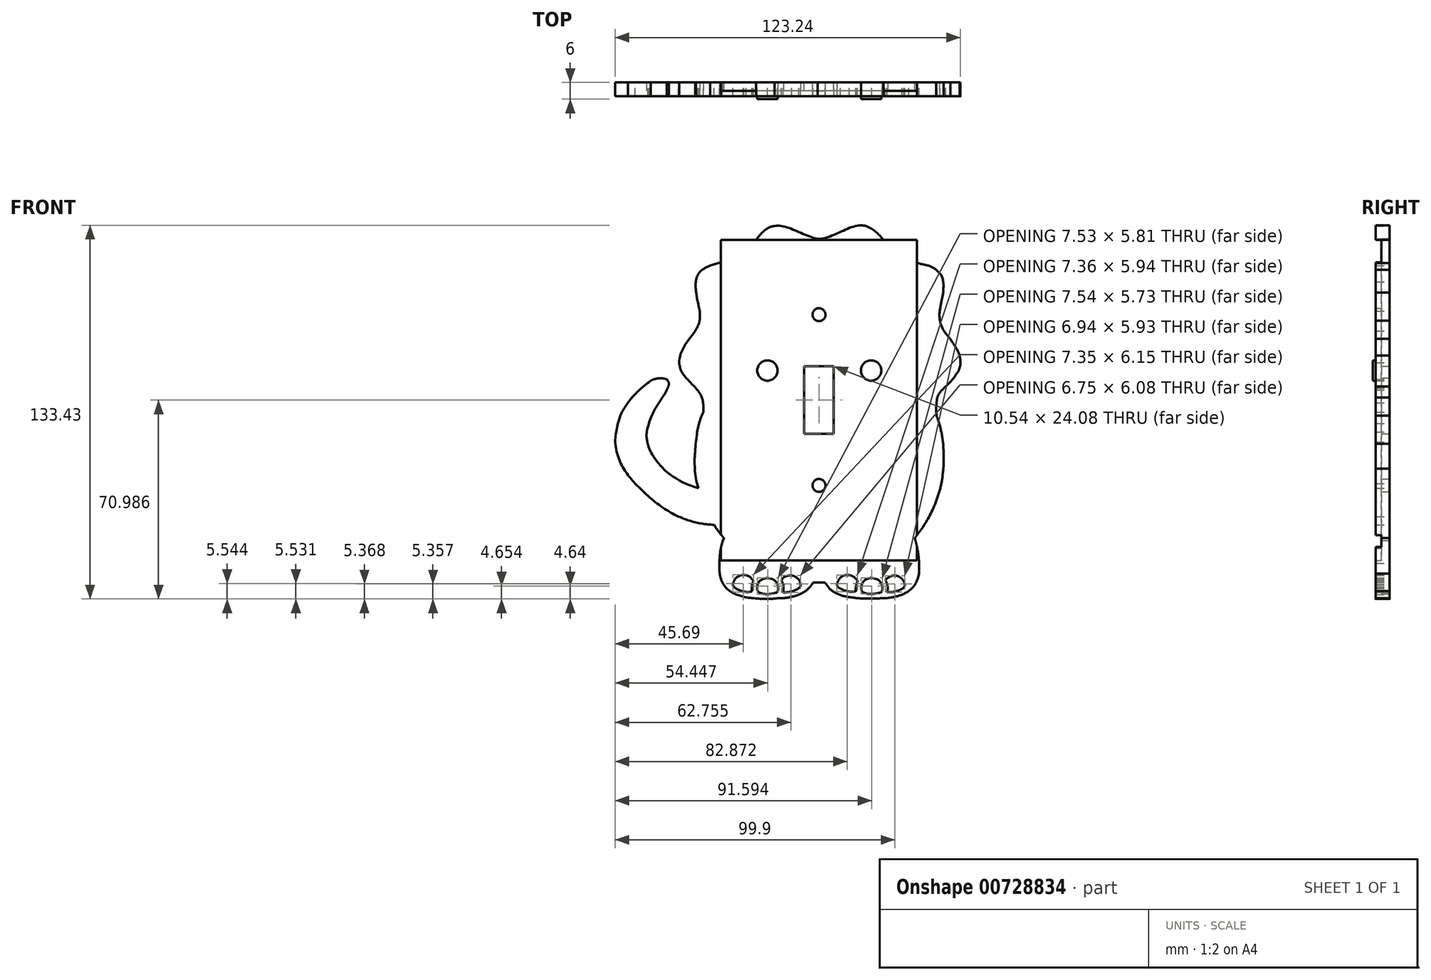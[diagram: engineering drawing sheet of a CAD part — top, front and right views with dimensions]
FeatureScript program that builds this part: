
annotation { "Feature Type Name" : "Feature", "Feature Type Description" : "" }
export const myFeature = defineFeature(function(context is Context, id is Id, definition is map)
    precondition{}
    {
        {
            var Q0;
            Q0=qCreatedBy(makeId("Front.planeOp"),FACE);
            var sketch = newSketch(context, id + "F0", { "sketchPlane" : qUnion([Q0])});
            skPoint(sketch, "E0.1.internal.snap0", {"position": v(2.99, 59.78) * mm});
            skFitSpline(sketch, "E0", {"points": [v(-7.47, 49.47) * mm, v(2.99, 58.9) * mm], "startDerivative": vector(10.46, 9.43) * mm, "endDerivative": vector(13.1, 0.69) * mm});
            skFitSpline(sketch, "E1", {"points": [v(2.99, 58.9) * mm, v(18.4, 54.3) * mm], "startDerivative": vector(13.1, 2.67) * mm, "endDerivative": vector(14.14, -2.41) * mm});
            skFitSpline(sketch, "E2", {"points": [v(18.4, 54.3) * mm, v(33.86, 59.2) * mm], "startDerivative": vector(12.35, -1.3) * mm, "endDerivative": vector(15.18, 0.82) * mm});
            skFitSpline(sketch, "E3", {"points": [v(33.86, 59.2) * mm, v(46.37, 48.8) * mm], "startDerivative": vector(18.66, -1.85) * mm, "endDerivative": vector(12.51, -10.4) * mm});
            skFitSpline(sketch, "E4", {"points": [v(46.37, 48.8) * mm, v(60.6, 43.21) * mm], "startDerivative": vector(10.09, -10.4) * mm, "endDerivative": vector(4.92, -7.38) * mm});
            skFitSpline(sketch, "E5", {"points": [v(60.6, 43.21) * mm, v(63.13, 35.15) * mm], "startDerivative": vector(4.1, -3.7) * mm, "endDerivative": vector(-1.85, -18.66) * mm});
            skFitSpline(sketch, "E6", {"points": [v(63.13, 35.15) * mm, v(62.04, 25.1) * mm], "startDerivative": vector(-2.67, -16) * mm, "endDerivative": vector(1.85, -9.02) * mm});
            skFitSpline(sketch, "E7", {"points": [v(62.04, 25.1) * mm, v(65.68, 18.57) * mm], "startDerivative": vector(0.44, -6.78) * mm, "endDerivative": vector(4.27, -4.63) * mm});
            skFitSpline(sketch, "E8", {"points": [v(65.68, 18.57) * mm, v(69.01, 12.62) * mm], "startDerivative": vector(3.45, -5.92) * mm, "endDerivative": vector(1.74, -6.36) * mm});
            skFitSpline(sketch, "E9", {"points": [v(69.01, 12.62) * mm, v(68.2, 6.5) * mm], "startDerivative": vector(1.74, -7.59) * mm, "endDerivative": vector(-3.49, -5.43) * mm});
            skFitSpline(sketch, "E10", {"points": [v(68.2, 6.5) * mm, v(64.02, 1.58) * mm], "startDerivative": vector(-3.8, -5.95) * mm, "endDerivative": vector(-4.82, -4.3) * mm});
            skFitSpline(sketch, "E11", {"points": [v(64.02, 1.58) * mm, v(61.05, -2.36) * mm], "startDerivative": vector(-3.18, -3.08) * mm, "endDerivative": vector(-2.05, -5.74) * mm});
            skFitSpline(sketch, "E12", {"points": [v(61.05, -2.36) * mm, v(60.74, -8.85) * mm], "startDerivative": vector(-1.44, -7.28) * mm, "endDerivative": vector(0.1, -6.15) * mm});
            skFitSpline(sketch, "E13", {"points": [v(60.74, -8.85) * mm, v(63.17, -18.86) * mm], "startDerivative": vector(4.2, -9.95) * mm, "endDerivative": vector(1.44, -10.87) * mm});
            skFitSpline(sketch, "E14", {"points": [v(63.17, -18.86) * mm, v(63.17, -27.79) * mm], "startDerivative": vector(0.41, -10.15) * mm, "endDerivative": vector(-1.13, -8.61) * mm});
            skFitSpline(sketch, "E15", {"points": [v(63.17, -27.79) * mm, v(61.32, -37.36) * mm], "startDerivative": vector(-0.92, -12.61) * mm, "endDerivative": vector(-2.97, -9.13) * mm});
            skFitSpline(sketch, "E16", {"points": [v(61.32, -37.36) * mm, v(53.02, -52.53) * mm], "startDerivative": vector(-6.56, -20.4) * mm, "endDerivative": vector(-9.74, -12.82) * mm});
            skFitSpline(sketch, "E17", {"points": [v(53.02, -52.53) * mm, v(54.52, -65.21) * mm], "startDerivative": vector(3.9, -13.33) * mm, "endDerivative": vector(-0.62, -12.82) * mm});
            skFitSpline(sketch, "E18", {"points": [v(54.52, -65.21) * mm, v(50.86, -71.38) * mm], "startDerivative": vector(-1.7, -7.76) * mm, "endDerivative": vector(-7.07, -5.24) * mm});
            skFitSpline(sketch, "E19", {"points": [v(50.86, -71.38) * mm, v(43.17, -73.94) * mm], "startDerivative": vector(-6.4, -4.5) * mm, "endDerivative": vector(-10.3, -1.38) * mm});
            skFitSpline(sketch, "E20", {"points": [v(43.17, -73.94) * mm, v(32.13, -73.94) * mm], "startDerivative": vector(-10.66, -0.22) * mm, "endDerivative": vector(-10.66, 1.1) * mm});
            skFitSpline(sketch, "E21", {"points": [v(32.13, -73.94) * mm, v(24.22, -71.74) * mm], "startDerivative": vector(-9.5, 1.45) * mm, "endDerivative": vector(-7.18, 4.79) * mm});
            skFitSpline(sketch, "E22", {"points": [v(24.22, -71.74) * mm, v(21.06, -68.38) * mm], "startDerivative": vector(-4.86, 2.54) * mm, "endDerivative": vector(-2.97, 4.57) * mm});
            skLineSegment(sketch, "E23", {"start": v(21.06, -68.38) * mm, "end": v(16.68, -68.38) * mm});
            skFitSpline(sketch, "E24", {"points": [v(16.68, -68.38) * mm, v(11.67, -72.71) * mm], "startDerivative": vector(-3.8, -7.05) * mm, "endDerivative": vector(-6.24, -2.76) * mm});
            skFitSpline(sketch, "E25", {"points": [v(11.67, -72.71) * mm, v(3.96, -73.97) * mm], "startDerivative": vector(-7.1, -2.4) * mm, "endDerivative": vector(-11.17, 0.22) * mm});
            skFitSpline(sketch, "E26", {"points": [v(3.96, -73.97) * mm, v(-7.2, -73.69) * mm], "startDerivative": vector(-11.87, -1.84) * mm, "endDerivative": vector(-8.77, 0.94) * mm});
            skFitSpline(sketch, "E27", {"points": [v(-7.2, -73.69) * mm, v(-15.71, -68.27) * mm], "startDerivative": vector(-9.72, 2.25) * mm, "endDerivative": vector(-5.3, 10.8) * mm});
            skFitSpline(sketch, "E28", {"points": [v(-15.71, -68.27) * mm, v(-16.73, -61.48) * mm], "startDerivative": vector(-2.76, 5.8) * mm, "endDerivative": vector(0.22, 7.03) * mm});
            skFitSpline(sketch, "E29", {"points": [v(-16.73, -61.48) * mm, v(-15.45, -53.36) * mm], "startDerivative": vector(0.5, 8.05) * mm, "endDerivative": vector(3.12, 9.06) * mm});
            skFitSpline(sketch, "E30", {"points": [v(-15.45, -53.36) * mm, v(-15.1, -52.54) * mm], "startDerivative": vector(0.34, 0.82) * mm, "endDerivative": vector(0.34, 0.82) * mm});
            skFitSpline(sketch, "E31", {"points": [v(-15.1, -52.54) * mm, v(-18.6, -47.79) * mm], "startDerivative": vector(-3.38, 4.36) * mm, "endDerivative": vector(-3.08, 5.43) * mm});
            skFitSpline(sketch, "E32", {"points": [v(-18.6, -47.79) * mm, v(-31.3, -44.81) * mm], "startDerivative": vector(-13.02, 0.56) * mm, "endDerivative": vector(-13.07, 5.8) * mm});
            skFitSpline(sketch, "E33", {"points": [v(-31.3, -44.81) * mm, v(-46.76, -33.1) * mm], "startDerivative": vector(-17.4, 8) * mm, "endDerivative": vector(-15.22, 15.29) * mm});
            skFitSpline(sketch, "E34", {"points": [v(-46.76, -33.1) * mm, v(-53.92, -18.17) * mm], "startDerivative": vector(-10.19, 11.75) * mm, "endDerivative": vector(-2.05, 21.53) * mm});
            skFitSpline(sketch, "E35", {"points": [v(-53.92, -18.17) * mm, v(-49.34, -4.22) * mm], "startDerivative": vector(1.03, 16.61) * mm, "endDerivative": vector(8.82, 10.87) * mm});
            skFitSpline(sketch, "E36", {"points": [v(-49.34, -4.22) * mm, v(-41.18, 3.68) * mm], "startDerivative": vector(7.03, 9.69) * mm, "endDerivative": vector(10, 7.44) * mm});
            skFitSpline(sketch, "E37", {"points": [v(-41.18, 3.68) * mm, v(-35.45, 4.13) * mm], "startDerivative": vector(8.3, 3.9) * mm, "endDerivative": vector(4.15, -1.46) * mm});
            skFitSpline(sketch, "E38", {"points": [v(-35.45, 4.13) * mm, v(-35.45, 0.39) * mm], "startDerivative": vector(3.66, -4.27) * mm, "endDerivative": vector(-1.83, -4.15) * mm});
            skFitSpline(sketch, "E39", {"points": [v(-35.45, 0.39) * mm, v(-41.87, -11.64) * mm], "startDerivative": vector(-6.42, -12.03) * mm, "endDerivative": vector(-4.51, -15.6) * mm});
            skFitSpline(sketch, "E40", {"points": [v(-41.87, -11.64) * mm, v(-42.28, -18.96) * mm], "startDerivative": vector(-3.66, -10) * mm, "endDerivative": vector(1.34, -6.59) * mm});
            skFitSpline(sketch, "E41", {"points": [v(-42.28, -18.96) * mm, v(-24.19, -34.7) * mm], "startDerivative": vector(2.68, -11.22) * mm, "endDerivative": vector(36.1, -9.88) * mm});
            skFitSpline(sketch, "E42", {"points": [v(-24.19, -34.7) * mm, v(-24.65, -14.6) * mm], "startDerivative": vector(-6.62, 19.8) * mm, "endDerivative": vector(2.32, 20.45) * mm});
            skFitSpline(sketch, "E43", {"points": [v(-24.65, -14.6) * mm, v(-22.43, -7.5) * mm], "startDerivative": vector(1.45, 7.54) * mm, "endDerivative": vector(3.2, 6.24) * mm});
            skFitSpline(sketch, "E44", {"points": [v(-22.43, -7.5) * mm, v(-25.04, 0.92) * mm], "startDerivative": vector(-0.15, 9.14) * mm, "endDerivative": vector(-8.85, 9.72) * mm});
            skFitSpline(sketch, "E45", {"points": [v(-25.04, 0.92) * mm, v(-31.08, 10.15) * mm], "startDerivative": vector(-17.7, 18.7) * mm, "endDerivative": vector(-2.32, 11.46) * mm});
            skFitSpline(sketch, "E46", {"points": [v(-31.08, 10.15) * mm, v(-25.33, 21.46) * mm], "startDerivative": vector(1.02, 15.52) * mm, "endDerivative": vector(6.24, 9.43) * mm});
            skFitSpline(sketch, "E47", {"points": [v(-25.33, 21.46) * mm, v(-23.69, 28.52) * mm], "startDerivative": vector(2.9, 5.51) * mm, "endDerivative": vector(-0.87, 12.62) * mm});
            skFitSpline(sketch, "E48", {"points": [v(-23.69, 28.52) * mm, v(-25.14, 38.96) * mm], "startDerivative": vector(-2.76, 12.04) * mm, "endDerivative": vector(0.73, 9.72) * mm});
            skFitSpline(sketch, "E49", {"points": [v(-25.14, 38.96) * mm, v(-19.97, 44.76) * mm], "startDerivative": vector(1.89, 12.9) * mm, "endDerivative": vector(6.38, 3.2) * mm});
            skFitSpline(sketch, "E50", {"points": [v(-19.97, 44.76) * mm, v(-9.67, 47.85) * mm], "startDerivative": vector(10.44, 3.77) * mm, "endDerivative": vector(8.7, 3.77) * mm});
            skFitSpline(sketch, "E51", {"points": [v(-9.67, 47.85) * mm, v(-7.47, 49.47) * mm], "startDerivative": vector(2.61, 0.73) * mm, "endDerivative": vector(2.2, 1.61) * mm});
            skFitSpline(sketch, "E52", {"points": [v(-11.9, -69.22) * mm, v(-8.18, -65.64) * mm], "startDerivative": vector(0.92, 4.72) * mm, "endDerivative": vector(8.61, 1.13) * mm});
            skFitSpline(sketch, "E53", {"points": [v(-7.94, -65.64) * mm, v(-4.56, -67.96) * mm], "startDerivative": vector(3.38, -0.41) * mm, "endDerivative": vector(2.77, -5.54) * mm});
            skFitSpline(sketch, "E54", {"points": [v(-4.56, -67.96) * mm, v(-5.03, -71.41) * mm], "startDerivative": vector(-2.46, -4.92) * mm, "endDerivative": vector(0.72, -2.77) * mm});
            skFitSpline(sketch, "E55", {"points": [v(-5.03, -71.41) * mm, v(-11.9, -69.22) * mm], "startDerivative": vector(-5.33, -3.7) * mm, "endDerivative": vector(-0.1, 4.1) * mm});
            skFitSpline(sketch, "E56", {"points": [v(-3.19, -71.14) * mm, v(0.43, -66.7) * mm], "startDerivative": vector(-1.85, 12) * mm, "endDerivative": vector(2.15, 0.62) * mm});
            skFitSpline(sketch, "E57", {"points": [v(0.43, -66.7) * mm, v(4.1, -71.51) * mm], "startDerivative": vector(14.25, -1.85) * mm, "endDerivative": vector(-0.72, -1.03) * mm});
            skFitSpline(sketch, "E58", {"points": [v(-3.19, -71.14) * mm, v(4.1, -71.51) * mm], "startDerivative": vector(3.38, -7.28) * mm, "endDerivative": vector(-0.92, 2.05) * mm});
            skFitSpline(sketch, "E59", {"points": [v(6.07, -71.93) * mm, v(12.2, -69.87) * mm], "startDerivative": vector(7.7, -0.1) * mm, "endDerivative": vector(2.77, 3.49) * mm});
            skFitSpline(sketch, "E60", {"points": [v(12.2, -69.87) * mm, v(9.05, -65.84) * mm], "startDerivative": vector(-0.1, 1.95) * mm, "endDerivative": vector(-11.18, 2.97) * mm});
            skFitSpline(sketch, "E61", {"points": [v(9.05, -65.84) * mm, v(5.46, -67.65) * mm], "startDerivative": vector(-4.3, -0.1) * mm, "endDerivative": vector(-2.56, -5.02) * mm});
            skFitSpline(sketch, "E62", {"points": [v(5.46, -67.65) * mm, v(6.07, -71.93) * mm], "startDerivative": vector(1.74, -3.59) * mm, "endDerivative": vector(-1.13, -7.8) * mm});
            skFitSpline(sketch, "E63", {"points": [v(25.28, -68.99) * mm, v(29.63, -65.74) * mm], "startDerivative": vector(-0.1, 1.64) * mm, "endDerivative": vector(10.25, -1.33) * mm});
            skFitSpline(sketch, "E64", {"points": [v(29.63, -65.74) * mm, v(32.63, -68.03) * mm], "startDerivative": vector(1.74, 0.1) * mm, "endDerivative": vector(2.36, -5.13) * mm});
            skFitSpline(sketch, "E65", {"points": [v(32.63, -68.03) * mm, v(32.12, -71.45) * mm], "startDerivative": vector(-1.23, -1.85) * mm, "endDerivative": vector(1.33, -3.8) * mm});
            skFitSpline(sketch, "E66", {"points": [v(25.28, -68.99) * mm, v(26.43, -70.55) * mm], "startDerivative": vector(-0.47, -2.95) * mm, "endDerivative": vector(1.33, -0.77) * mm});
            skFitSpline(sketch, "E67", {"points": [v(26.43, -70.55) * mm, v(32.12, -71.45) * mm], "startDerivative": vector(6.56, -3.44) * mm, "endDerivative": vector(4.83, 1.36) * mm});
            skFitSpline(sketch, "E68", {"points": [v(33.98, -71.13) * mm, v(37.7, -66.72) * mm], "startDerivative": vector(-0.87, 3.08) * mm, "endDerivative": vector(11.33, 0.77) * mm});
            skFitSpline(sketch, "E69", {"points": [v(37.7, -66.72) * mm, v(41.35, -71.35) * mm], "startDerivative": vector(12.87, -1.54) * mm, "endDerivative": vector(-0.46, -2.2) * mm});
            skFitSpline(sketch, "E70", {"points": [v(33.98, -71.13) * mm, v(41.35, -71.35) * mm], "startDerivative": vector(2.82, -7.13) * mm, "endDerivative": vector(-1.7, 2.36) * mm});
            skFitSpline(sketch, "E71", {"points": [v(42.5, -67.52) * mm, v(48.5, -67.08) * mm], "startDerivative": vector(1.23, 1.18) * mm, "endDerivative": vector(9.59, -8.25) * mm});
            skFitSpline(sketch, "E72", {"points": [v(48.5, -67.08) * mm, v(49.09, -70.2) * mm], "startDerivative": vector(1.9, -2.56) * mm, "endDerivative": vector(-2.61, -3.38) * mm});
            skFitSpline(sketch, "E73", {"points": [v(49.09, -70.2) * mm, v(43.1, -71.81) * mm], "startDerivative": vector(-5.02, -3.49) * mm, "endDerivative": vector(-7.74, 0.46) * mm});
            skFitSpline(sketch, "E74", {"points": [v(42.5, -67.52) * mm, v(43.1, -71.81) * mm], "startDerivative": vector(1.54, -2.56) * mm, "endDerivative": vector(-1.9, -4.77) * mm});
            skEllipse(sketch, "E75", {"center": v(14.47, -19.48) * mm, "majorRadius": 3.3 * mm, "minorRadius": 2.54 * mm, "majorAxis": v(-0.41, 0.91)});
            skEllipse(sketch, "E76", {"center": v(23.22, -19.68) * mm, "majorRadius": 3.36 * mm, "minorRadius": 2.42 * mm, "majorAxis": v(0.55, 0.84)});
            skFitSpline(sketch, "E77", {"points": [v(18.8, -2.75) * mm, v(15.96, -12.8) * mm], "startDerivative": vector(-5.6, -9.76) * mm, "endDerivative": vector(1.95, -11.34) * mm});
            skFitSpline(sketch, "E78", {"points": [v(18.8, -2.75) * mm, v(21.85, -12.67) * mm], "startDerivative": vector(5.6, -8.54) * mm, "endDerivative": vector(-1.1, -12.68) * mm});
            skFitSpline(sketch, "E79", {"points": [v(15.96, -12.8) * mm, v(21.85, -12.67) * mm], "startDerivative": vector(9.63, -9.88) * mm, "endDerivative": vector(2.32, 2.68) * mm});
            skCircle(sketch, "E80", {"center": v(37.44, 7.3) * mm, "radius": 8.13 * mm});
            skPoint(sketch, "E80.first.point", {"position": v(35.22, 15.12) * mm});
            skPoint(sketch, "E80.second.point", {"position": v(39.45, -0.57) * mm});
            skPoint(sketch, "E80.third.point", {"position": v(31.4, 1.86) * mm});
            skCircle(sketch, "E81", {"center": v(0.43, 7.3) * mm, "radius": 8.13 * mm});
            skFitSpline(sketch, "E82", {"points": [v(-0.95, 42.83) * mm, v(9.53, 27.7) * mm], "startDerivative": vector(11.46, -7.32) * mm, "endDerivative": vector(3.41, -21.46) * mm});
            skFitSpline(sketch, "E83", {"points": [v(-0.95, 42.83) * mm, v(-0.95, 25.1) * mm], "startDerivative": vector(-9.02, -23.41) * mm, "endDerivative": vector(2.68, -10.73) * mm});
            skFitSpline(sketch, "E84", {"points": [v(-0.95, 25.1) * mm, v(9.53, 27.7) * mm], "startDerivative": vector(8.54, -7.56) * mm, "endDerivative": vector(7.07, 18.3) * mm});
            skFitSpline(sketch, "E85", {"points": [v(39.04, 42.83) * mm, v(37.99, 24.38) * mm], "startDerivative": vector(7.56, -22.44) * mm, "endDerivative": vector(-4.88, -4.63) * mm});
            skFitSpline(sketch, "E86", {"points": [v(39.04, 42.83) * mm, v(28.31, 28.2) * mm], "startDerivative": vector(-5.6, 0.24) * mm, "endDerivative": vector(-4.15, -21.95) * mm});
            skFitSpline(sketch, "E87", {"points": [v(28.31, 28.2) * mm, v(37.99, 24.38) * mm], "startDerivative": vector(6.59, -21.22) * mm, "endDerivative": vector(4.88, 3.66) * mm});
            skFitSpline(sketch, "E88", {"points": [v(-8.18, -65.64) * mm, v(-7.94, -65.64) * mm], "startDerivative": vector(0.24, 0) * mm, "endDerivative": vector(0.24, 0) * mm});
            skSolve(sketch);
        }
        {
            var Q0;
            Q0 = qSketchRegion(id + "F0", true);
            extrude(context, id + "F1", {"entities" : qUnion([Q0]), "depth" : 5 * mm, "offsetDistance" : 25 * mm});
        }
        {
            var Q0;
            Q0=makeQuery(id+"F1.opExtrude","CAP_FACE",FACE,{"disambiguationData":[OSD([sQuery(id+"F0.wireOp",EDGE,"E0"),sQuery(id+"F0.wireOp",EDGE,"E1"),sQuery(id+"F0.wireOp",EDGE,"E2"),sQuery(id+"F0.wireOp",EDGE,"E3"),sQuery(id+"F0.wireOp",EDGE,"E4"),sQuery(id+"F0.wireOp",EDGE,"E5"),sQuery(id+"F0.wireOp",EDGE,"E6"),sQuery(id+"F0.wireOp",EDGE,"E7"),sQuery(id+"F0.wireOp",EDGE,"E8"),sQuery(id+"F0.wireOp",EDGE,"E9"),sQuery(id+"F0.wireOp",EDGE,"E10"),sQuery(id+"F0.wireOp",EDGE,"E11"),sQuery(id+"F0.wireOp",EDGE,"E12"),sQuery(id+"F0.wireOp",EDGE,"E13"),sQuery(id+"F0.wireOp",EDGE,"E14"),sQuery(id+"F0.wireOp",EDGE,"E15"),sQuery(id+"F0.wireOp",EDGE,"E16"),sQuery(id+"F0.wireOp",EDGE,"E17"),sQuery(id+"F0.wireOp",EDGE,"E18"),sQuery(id+"F0.wireOp",EDGE,"E19"),sQuery(id+"F0.wireOp",EDGE,"E20"),sQuery(id+"F0.wireOp",EDGE,"E21"),sQuery(id+"F0.wireOp",EDGE,"E22"),sQuery(id+"F0.wireOp",EDGE,"E23"),sQuery(id+"F0.wireOp",EDGE,"E24"),sQuery(id+"F0.wireOp",EDGE,"E25"),sQuery(id+"F0.wireOp",EDGE,"E26"),sQuery(id+"F0.wireOp",EDGE,"E27"),sQuery(id+"F0.wireOp",EDGE,"E28"),sQuery(id+"F0.wireOp",EDGE,"E29"),sQuery(id+"F0.wireOp",EDGE,"E30"),sQuery(id+"F0.wireOp",EDGE,"E31"),sQuery(id+"F0.wireOp",EDGE,"E32"),sQuery(id+"F0.wireOp",EDGE,"E33"),sQuery(id+"F0.wireOp",EDGE,"E34"),sQuery(id+"F0.wireOp",EDGE,"E35"),sQuery(id+"F0.wireOp",EDGE,"E36"),sQuery(id+"F0.wireOp",EDGE,"E37"),sQuery(id+"F0.wireOp",EDGE,"E38"),sQuery(id+"F0.wireOp",EDGE,"E39"),sQuery(id+"F0.wireOp",EDGE,"E40"),sQuery(id+"F0.wireOp",EDGE,"E41"),sQuery(id+"F0.wireOp",EDGE,"E42"),sQuery(id+"F0.wireOp",EDGE,"E43"),sQuery(id+"F0.wireOp",EDGE,"E44"),sQuery(id+"F0.wireOp",EDGE,"E45"),sQuery(id+"F0.wireOp",EDGE,"E46"),sQuery(id+"F0.wireOp",EDGE,"E47"),sQuery(id+"F0.wireOp",EDGE,"E48"),sQuery(id+"F0.wireOp",EDGE,"E49"),sQuery(id+"F0.wireOp",EDGE,"E50"),sQuery(id+"F0.wireOp",EDGE,"E51"),sQuery(id+"F0.wireOp",EDGE,"E52"),sQuery(id+"F0.wireOp",EDGE,"E53"),sQuery(id+"F0.wireOp",EDGE,"E54"),sQuery(id+"F0.wireOp",EDGE,"E55"),sQuery(id+"F0.wireOp",EDGE,"E56"),sQuery(id+"F0.wireOp",EDGE,"E57"),sQuery(id+"F0.wireOp",EDGE,"E58"),sQuery(id+"F0.wireOp",EDGE,"E59"),sQuery(id+"F0.wireOp",EDGE,"E60"),sQuery(id+"F0.wireOp",EDGE,"E61"),sQuery(id+"F0.wireOp",EDGE,"E62"),sQuery(id+"F0.wireOp",EDGE,"E63"),sQuery(id+"F0.wireOp",EDGE,"E64"),sQuery(id+"F0.wireOp",EDGE,"E65"),sQuery(id+"F0.wireOp",EDGE,"E66"),sQuery(id+"F0.wireOp",EDGE,"E67"),sQuery(id+"F0.wireOp",EDGE,"E68"),sQuery(id+"F0.wireOp",EDGE,"E69"),sQuery(id+"F0.wireOp",EDGE,"E70"),sQuery(id+"F0.wireOp",EDGE,"E71"),sQuery(id+"F0.wireOp",EDGE,"E72"),sQuery(id+"F0.wireOp",EDGE,"E73"),sQuery(id+"F0.wireOp",EDGE,"E74"),sQuery(id+"F0.wireOp",EDGE,"E75"),sQuery(id+"F0.wireOp",EDGE,"E76"),sQuery(id+"F0.wireOp",EDGE,"E77"),sQuery(id+"F0.wireOp",EDGE,"E78"),sQuery(id+"F0.wireOp",EDGE,"E79"),sQuery(id+"F0.wireOp",EDGE,"E80"),sQuery(id+"F0.wireOp",EDGE,"E81"),sQuery(id+"F0.wireOp",EDGE,"E82"),sQuery(id+"F0.wireOp",EDGE,"E83"),sQuery(id+"F0.wireOp",EDGE,"E84"),sQuery(id+"F0.wireOp",EDGE,"E85"),sQuery(id+"F0.wireOp",EDGE,"E86"),sQuery(id+"F0.wireOp",EDGE,"E87"),sQuery(id+"F0.wireOp",EDGE,"E88")])],"isStart":true});
            var sketch = newSketch(context, id + "F2", { "sketchPlane" : qUnion([Q0])});
            skLineSegment(sketch, "E89.bottom", {"start": v(-24.1, 8.79) * mm, "end": v(-24.1, -15.3) * mm});
            skLineSegment(sketch, "E89.top", {"start": v(-13.57, 8.79) * mm, "end": v(-13.57, -15.3) * mm});
            skLineSegment(sketch, "E89.left", {"start": v(-24.1, 8.79) * mm, "end": v(-13.57, 8.79) * mm});
            skLineSegment(sketch, "E89.right", {"start": v(-24.1, -15.3) * mm, "end": v(-13.57, -15.3) * mm});
            skCircle(sketch, "E90", {"center": v(-18.84, -33.73) * mm, "radius": 2.31 * mm});
            skLineSegment(sketch, "E91", {"start": v(-55.14, -3.25) * mm, "end": v(34, -3.25) * mm, "construction": true});
            skLineSegment(sketch, "E92", {"start": v(-53.8, -3.25) * mm, "end": v(-53.8, -60.49) * mm});
            skLineSegment(sketch, "E93", {"start": v(-53.8, -60.49) * mm, "end": v(16.19, -60.49) * mm});
            skLineSegment(sketch, "E94", {"start": v(16.19, -60.49) * mm, "end": v(16.19, -3.25) * mm});
            skLineSegment(sketch, "E95.MirrorCS", {"start": v(-53.8, -3.25) * mm, "end": v(-53.8, 53.98) * mm});
            skLineSegment(sketch, "E96.MirrorCS", {"start": v(-53.8, 53.98) * mm, "end": v(16.19, 53.98) * mm});
            skLineSegment(sketch, "E97.MirrorCS", {"start": v(16.19, 53.98) * mm, "end": v(16.19, -3.25) * mm});
            skCircle(sketch, "E98.MirrorC", {"center": v(-18.84, 27.23) * mm, "radius": 2.31 * mm});
            skSolve(sketch);
        }
        {
            var Q0;
            Q0=makeQuery(id+"F2.imprint","IMPRINT",FACE,{"disambiguationData":[TD([[makeQuery(id+"F2.imprint","IMPRINT",EDGE,{"derivedFrom":sQuery(id+"F2.wireOp",EDGE,"E89.bottom")}),1.0]])]});
            var Q1;
            Q1=makeQuery(id+"F2.imprint","IMPRINT",FACE,{"disambiguationData":[TD([[makeQuery(id+"F2.imprint","IMPRINT",EDGE,{"derivedFrom":sQuery(id+"F2.wireOp",EDGE,"E98.MirrorC")}),-1.0]])]});
            var Q2;
            Q2=makeQuery(id+"F2.imprint","IMPRINT",FACE,{"disambiguationData":[TD([[makeQuery(id+"F2.imprint","IMPRINT",EDGE,{"derivedFrom":sQuery(id+"F2.wireOp",EDGE,"E90")}),1.0]])]});
            extrude(context, id + "F3", {"entities" : qUnion([Q0, Q1, Q2]), "operationType" : NewBodyOperationType.REMOVE, "oppositeDirection" : true, "depth" : 25 * mm, "offsetDistance" : 25 * mm});
        }
        {
            var Q0;
            {var subQ0=makeQuery(id+"F1.opExtrude","CAP_EDGE",EDGE,{"disambiguationData":[OSD([sQuery(id+"F0.wireOp",EDGE,"E51")])],"isStart":true});Q0=makeQuery(id+"F2.imprint","IMPRINT",FACE,{"disambiguationData":[TD([[makeQuery(id+"F2.imprint","IMPRINT",EDGE,{"derivedFrom":subQ0}),-1.0]])]});}
            var Q1;
            {var subQ0=sQuery(id+"F2.wireOp",EDGE,"E96.MirrorCS");var subQ1=sQuery(id+"F2.wireOp",EDGE,"E95.MirrorCS");var subQ2=makeQuery(id+"F2.imprint","INTERSECT",VERTEX,{"derivedFrom":[subQ1,subQ0]});Q1=makeQuery(id+"F2.imprint","IMPRINT",FACE,{"disambiguationData":[TD([[makeQuery(id+"F2.imprint","IMPRINT",EDGE,{"disambiguationData":[TD([[subQ2,1.0]])],"derivedFrom":subQ1}),-1.0]])]});}
            var Q2;
            Q2=makeQuery(id+"F2.imprint","IMPRINT",FACE,{"disambiguationData":[TD([[makeQuery(id+"F2.imprint","IMPRINT",EDGE,{"derivedFrom":sQuery(id+"F2.wireOp",EDGE,"E89.bottom")}),-1.0]])]});
            extrude(context, id + "F4", {"entities" : qUnion([Q0, Q1, Q2]), "operationType" : NewBodyOperationType.ADD, "oppositeDirection" : true, "depth" : 3 * mm, "offsetDistance" : 25 * mm});
        }
        {
            var Q0;
            Q0=makeQuery(id+"F2.imprint","IMPRINT",FACE,{"disambiguationData":[TD([[makeQuery(id+"F2.imprint","IMPRINT",EDGE,{"derivedFrom":makeQuery(id+"F1.opExtrude","CAP_EDGE",EDGE,{"disambiguationData":[OSD([sQuery(id+"F0.wireOp",EDGE,"E85")])],"isStart":true})}),1.0]])]});
            var Q1;
            Q1=makeQuery(id+"F2.imprint","IMPRINT",FACE,{"disambiguationData":[TD([[makeQuery(id+"F2.imprint","IMPRINT",EDGE,{"derivedFrom":makeQuery(id+"F1.opExtrude","CAP_EDGE",EDGE,{"disambiguationData":[OSD([sQuery(id+"F0.wireOp",EDGE,"E82")])],"isStart":true})}),1.0]])]});
            var Q2;
            Q2=makeQuery(id+"F2.imprint","IMPRINT",FACE,{"disambiguationData":[TD([[makeQuery(id+"F2.imprint","IMPRINT",EDGE,{"derivedFrom":makeQuery(id+"F1.opExtrude","CAP_EDGE",EDGE,{"disambiguationData":[OSD([sQuery(id+"F0.wireOp",EDGE,"E81")])],"isStart":true})}),-1.0]])]});
            var Q3;
            Q3=makeQuery(id+"F2.imprint","IMPRINT",FACE,{"disambiguationData":[TD([[makeQuery(id+"F2.imprint","IMPRINT",EDGE,{"derivedFrom":makeQuery(id+"F1.opExtrude","CAP_EDGE",EDGE,{"disambiguationData":[OSD([sQuery(id+"F0.wireOp",EDGE,"E80")])],"isStart":true})}),-1.0]])]});
            var Q4;
            Q4=makeQuery(id+"F2.imprint","IMPRINT",FACE,{"disambiguationData":[TD([[makeQuery(id+"F2.imprint","IMPRINT",EDGE,{"derivedFrom":makeQuery(id+"F1.opExtrude","CAP_EDGE",EDGE,{"disambiguationData":[OSD([sQuery(id+"F0.wireOp",EDGE,"E76")])],"isStart":true})}),-1.0]])]});
            var Q5;
            Q5=makeQuery(id+"F2.imprint","IMPRINT",FACE,{"disambiguationData":[TD([[makeQuery(id+"F2.imprint","IMPRINT",EDGE,{"derivedFrom":makeQuery(id+"F1.opExtrude","CAP_EDGE",EDGE,{"disambiguationData":[OSD([sQuery(id+"F0.wireOp",EDGE,"E75")])],"isStart":true})}),-1.0]])]});
            extrude(context, id + "F5", {"entities" : qUnion([Q0, Q1, Q2, Q3, Q4, Q5]), "operationType" : NewBodyOperationType.ADD, "oppositeDirection" : true, "depth" : 3 * mm, "offsetDistance" : 25 * mm});
        }
        {
            var Q0;
            Q0=makeQuery(id+"F1.opExtrude","CAP_FACE",FACE,{"disambiguationData":[OSD([sQuery(id+"F0.wireOp",EDGE,"E0"),sQuery(id+"F0.wireOp",EDGE,"E1"),sQuery(id+"F0.wireOp",EDGE,"E2"),sQuery(id+"F0.wireOp",EDGE,"E3"),sQuery(id+"F0.wireOp",EDGE,"E4"),sQuery(id+"F0.wireOp",EDGE,"E5"),sQuery(id+"F0.wireOp",EDGE,"E6"),sQuery(id+"F0.wireOp",EDGE,"E7"),sQuery(id+"F0.wireOp",EDGE,"E8"),sQuery(id+"F0.wireOp",EDGE,"E9"),sQuery(id+"F0.wireOp",EDGE,"E10"),sQuery(id+"F0.wireOp",EDGE,"E11"),sQuery(id+"F0.wireOp",EDGE,"E12"),sQuery(id+"F0.wireOp",EDGE,"E13"),sQuery(id+"F0.wireOp",EDGE,"E14"),sQuery(id+"F0.wireOp",EDGE,"E15"),sQuery(id+"F0.wireOp",EDGE,"E16"),sQuery(id+"F0.wireOp",EDGE,"E17"),sQuery(id+"F0.wireOp",EDGE,"E18"),sQuery(id+"F0.wireOp",EDGE,"E19"),sQuery(id+"F0.wireOp",EDGE,"E20"),sQuery(id+"F0.wireOp",EDGE,"E21"),sQuery(id+"F0.wireOp",EDGE,"E22"),sQuery(id+"F0.wireOp",EDGE,"E23"),sQuery(id+"F0.wireOp",EDGE,"E24"),sQuery(id+"F0.wireOp",EDGE,"E25"),sQuery(id+"F0.wireOp",EDGE,"E26"),sQuery(id+"F0.wireOp",EDGE,"E27"),sQuery(id+"F0.wireOp",EDGE,"E28"),sQuery(id+"F0.wireOp",EDGE,"E29"),sQuery(id+"F0.wireOp",EDGE,"E30"),sQuery(id+"F0.wireOp",EDGE,"E31"),sQuery(id+"F0.wireOp",EDGE,"E32"),sQuery(id+"F0.wireOp",EDGE,"E33"),sQuery(id+"F0.wireOp",EDGE,"E34"),sQuery(id+"F0.wireOp",EDGE,"E35"),sQuery(id+"F0.wireOp",EDGE,"E36"),sQuery(id+"F0.wireOp",EDGE,"E37"),sQuery(id+"F0.wireOp",EDGE,"E38"),sQuery(id+"F0.wireOp",EDGE,"E39"),sQuery(id+"F0.wireOp",EDGE,"E40"),sQuery(id+"F0.wireOp",EDGE,"E41"),sQuery(id+"F0.wireOp",EDGE,"E42"),sQuery(id+"F0.wireOp",EDGE,"E43"),sQuery(id+"F0.wireOp",EDGE,"E44"),sQuery(id+"F0.wireOp",EDGE,"E45"),sQuery(id+"F0.wireOp",EDGE,"E46"),sQuery(id+"F0.wireOp",EDGE,"E47"),sQuery(id+"F0.wireOp",EDGE,"E48"),sQuery(id+"F0.wireOp",EDGE,"E49"),sQuery(id+"F0.wireOp",EDGE,"E50"),sQuery(id+"F0.wireOp",EDGE,"E51"),sQuery(id+"F0.wireOp",EDGE,"E52"),sQuery(id+"F0.wireOp",EDGE,"E53"),sQuery(id+"F0.wireOp",EDGE,"E54"),sQuery(id+"F0.wireOp",EDGE,"E55"),sQuery(id+"F0.wireOp",EDGE,"E56"),sQuery(id+"F0.wireOp",EDGE,"E57"),sQuery(id+"F0.wireOp",EDGE,"E58"),sQuery(id+"F0.wireOp",EDGE,"E59"),sQuery(id+"F0.wireOp",EDGE,"E60"),sQuery(id+"F0.wireOp",EDGE,"E61"),sQuery(id+"F0.wireOp",EDGE,"E62"),sQuery(id+"F0.wireOp",EDGE,"E63"),sQuery(id+"F0.wireOp",EDGE,"E64"),sQuery(id+"F0.wireOp",EDGE,"E65"),sQuery(id+"F0.wireOp",EDGE,"E66"),sQuery(id+"F0.wireOp",EDGE,"E67"),sQuery(id+"F0.wireOp",EDGE,"E68"),sQuery(id+"F0.wireOp",EDGE,"E69"),sQuery(id+"F0.wireOp",EDGE,"E70"),sQuery(id+"F0.wireOp",EDGE,"E71"),sQuery(id+"F0.wireOp",EDGE,"E72"),sQuery(id+"F0.wireOp",EDGE,"E73"),sQuery(id+"F0.wireOp",EDGE,"E74"),sQuery(id+"F0.wireOp",EDGE,"E75"),sQuery(id+"F0.wireOp",EDGE,"E76"),sQuery(id+"F0.wireOp",EDGE,"E77"),sQuery(id+"F0.wireOp",EDGE,"E78"),sQuery(id+"F0.wireOp",EDGE,"E79"),sQuery(id+"F0.wireOp",EDGE,"E80"),sQuery(id+"F0.wireOp",EDGE,"E81"),sQuery(id+"F0.wireOp",EDGE,"E82"),sQuery(id+"F0.wireOp",EDGE,"E83"),sQuery(id+"F0.wireOp",EDGE,"E84"),sQuery(id+"F0.wireOp",EDGE,"E85"),sQuery(id+"F0.wireOp",EDGE,"E86"),sQuery(id+"F0.wireOp",EDGE,"E87"),sQuery(id+"F0.wireOp",EDGE,"E88")])],"isStart":false});
            var sketch = newSketch(context, id + "F6", { "sketchPlane" : qUnion([Q0])});
            skCircle(sketch, "E99", {"center": v(0.43, 7.3) * mm, "radius": 3.63 * mm});
            skCircle(sketch, "E100", {"center": v(37.44, 7.3) * mm, "radius": 3.63 * mm});
            skSolve(sketch);
        }
        {
            var Q0;
            Q0=makeQuery(id+"F6.imprint","IMPRINT",FACE,{"disambiguationData":[TD([[makeQuery(id+"F6.imprint","IMPRINT",EDGE,{"derivedFrom":sQuery(id+"F6.wireOp",EDGE,"E99")}),1.0]])]});
            var Q1;
            Q1=makeQuery(id+"F6.imprint","IMPRINT",FACE,{"disambiguationData":[TD([[makeQuery(id+"F6.imprint","IMPRINT",EDGE,{"derivedFrom":sQuery(id+"F6.wireOp",EDGE,"E100")}),1.0]])]});
            extrude(context, id + "F7", {"entities" : qUnion([Q0, Q1]), "depth" : 1 * mm, "offsetDistance" : 25 * mm});
        }
    });
